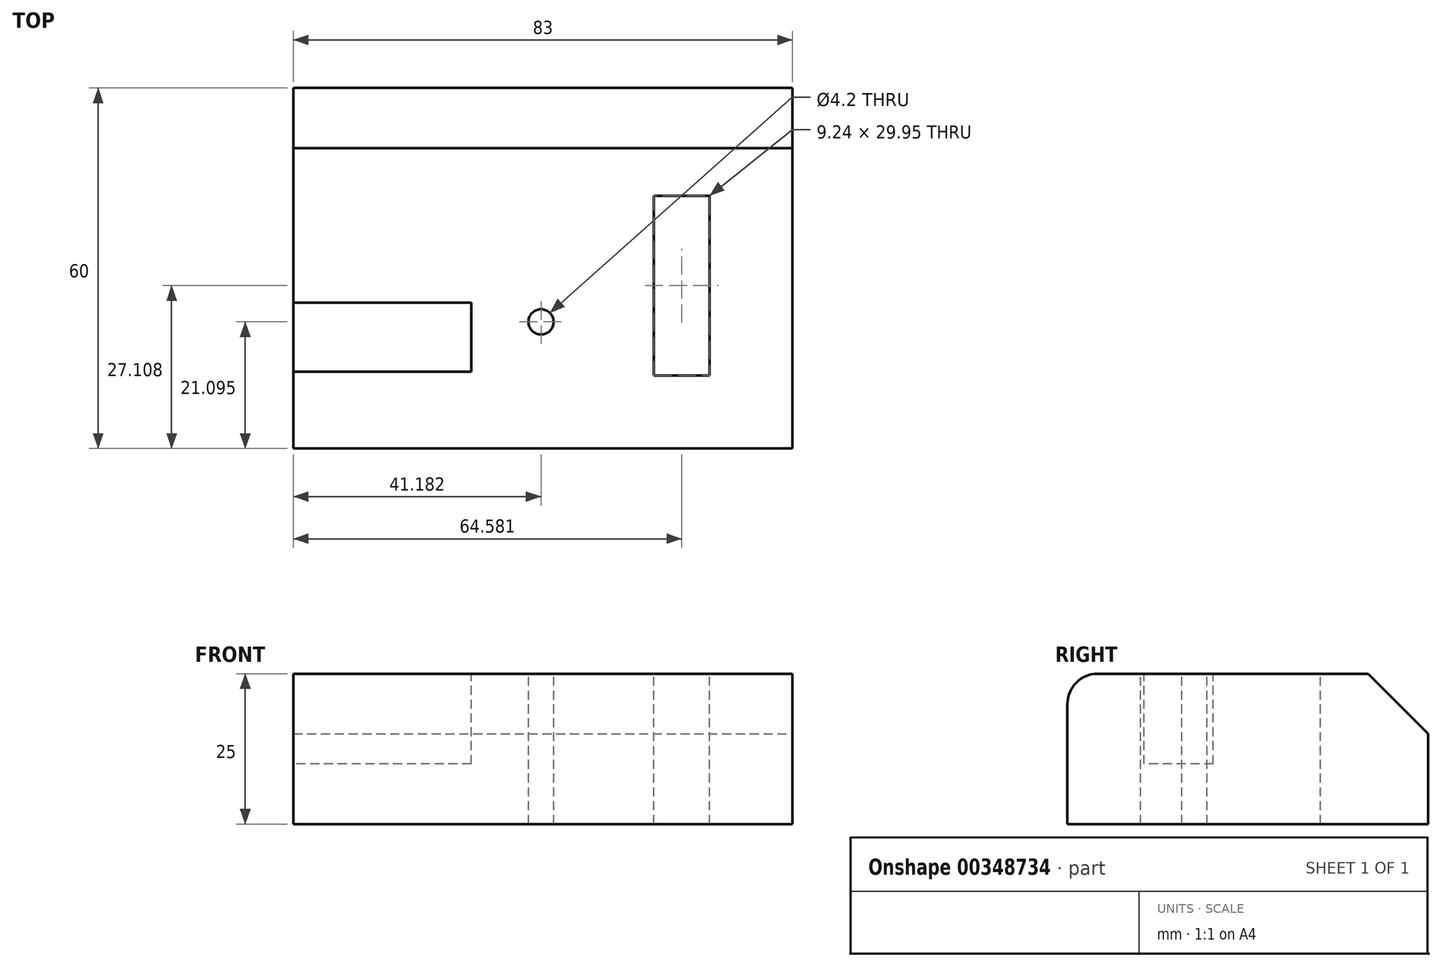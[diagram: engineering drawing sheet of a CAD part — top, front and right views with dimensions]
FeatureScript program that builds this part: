
annotation { "Feature Type Name" : "Feature", "Feature Type Description" : "" }
export const myFeature = defineFeature(function(context is Context, id is Id, definition is map)
    precondition{}
    {
        {
            var Q0;
            Q0=qCreatedBy(makeId("Top.planeOp"),FACE);
            var sketch = newSketch(context, id + "F0", { "sketchPlane" : qUnion([Q0])});
            skLineSegment(sketch, "E0.bottom", {"start": v(0, 60) * mm, "end": v(83, 60) * mm});
            skLineSegment(sketch, "E0.top", {"start": v(0, 0) * mm, "end": v(83, 0) * mm});
            skLineSegment(sketch, "E0.left", {"start": v(0, 60) * mm, "end": v(0, 0) * mm});
            skLineSegment(sketch, "E0.right", {"start": v(83, 60) * mm, "end": v(83, 0) * mm});
            skSolve(sketch);
        }
        {
            var Q0;
            Q0=makeQuery(id+"F0.imprint","IMPRINT",FACE,{"disambiguationData":[TD([[makeQuery(id+"F0.imprint","IMPRINT",EDGE,{"derivedFrom":sQuery(id+"F0.wireOp",EDGE,"E0.bottom")}),-1.0]])]});
            extrude(context, id + "F1", {"entities" : qUnion([Q0]), "depth" : 25 * mm});
        }
        {
            var Q0;
            Q0=makeQuery(id+"F1.opExtrude","CAP_EDGE",EDGE,{"disambiguationData":[OSD([sQuery(id+"F0.wireOp",EDGE,"E0.top")])],"isStart":false});
            fillet(context, id + "F2", {"entities" : qUnion([Q0]), "radius" : 5 * mm, "tangentPropagation" : true, "allowEdgeOverflow" : false});
        }
        {
            var Q0;
            Q0=makeQuery(id+"F1.opExtrude","CAP_EDGE",EDGE,{"disambiguationData":[OSD([sQuery(id+"F0.wireOp",EDGE,"E0.bottom")])],"isStart":false});
            chamfer(context, id + "F3", {"entities" : qUnion([Q0]), "width" : 10 * mm, "tangentPropagation" : true});
        }
        {
            var Q0;
            Q0=makeQuery(id+"F1.opExtrude","CAP_FACE",FACE,{"disambiguationData":[OSD([sQuery(id+"F0.wireOp",EDGE,"E0.bottom"),sQuery(id+"F0.wireOp",EDGE,"E0.top"),sQuery(id+"F0.wireOp",EDGE,"E0.left"),sQuery(id+"F0.wireOp",EDGE,"E0.right")])],"isStart":false});
            var sketch = newSketch(context, id + "F4", { "sketchPlane" : qUnion([Q0])});
            skPoint(sketch, "E1", {"position": v(41.18, 21.1) * mm});
            skSolve(sketch);
        }
        {
            var Q0;
            Q0=sQuery(id+"F4.wireOp",VERTEX,"E1");
            var Q1;
            Q1=makeQuery(id+"F1.opExtrude","SWEPT_BODY",BODY,{"disambiguationData":[OSD([sQuery(id+"F0.wireOp",EDGE,"E0.bottom"),sQuery(id+"F0.wireOp",EDGE,"E0.top"),sQuery(id+"F0.wireOp",EDGE,"E0.left"),sQuery(id+"F0.wireOp",EDGE,"E0.right")])]});
            hole(context, id + "F5", {"style" : HoleStyle.SIMPLE, "endStyle" : HoleEndStyle.THROUGH, "standardTappedOrClearance" : lookupTablePath({ "standard" : "ISO", "engagement" : "75%", "pitch" : "0.8 mm", "size" : "M5", "type" : "Tapped" }), "standardBlindInLast" : lookupTablePath({ "standard" : "ISO", "engagement" : "75%", "pitch" : "0.8 mm", "size" : "M5", "type" : "Tapped" }), "holeDiameter" : 4.2 * mm, "showTappedDepth" : true, "isTappedThrough" : true, "tappedDepth" : 12 * mm, "tapClearance" : 3, "locations" : qUnion([Q0]), "scope" : qUnion([Q1]), "majorDiameter" : 5 * mm});
        }
        {
            var Q0;
            Q0=makeQuery(id+"F1.opExtrude","CAP_FACE",FACE,{"disambiguationData":[OSD([sQuery(id+"F0.wireOp",EDGE,"E0.bottom"),sQuery(id+"F0.wireOp",EDGE,"E0.top"),sQuery(id+"F0.wireOp",EDGE,"E0.left"),sQuery(id+"F0.wireOp",EDGE,"E0.right")])],"isStart":false});
            var sketch = newSketch(context, id + "F6", { "sketchPlane" : qUnion([Q0])});
            skLineSegment(sketch, "E2.bottom", {"start": v(59.96, 12.14) * mm, "end": v(69.2, 12.14) * mm});
            skLineSegment(sketch, "E2.top", {"start": v(59.96, 42.08) * mm, "end": v(69.2, 42.08) * mm});
            skLineSegment(sketch, "E2.left", {"start": v(59.96, 12.14) * mm, "end": v(59.96, 42.08) * mm});
            skLineSegment(sketch, "E2.right", {"start": v(69.2, 12.14) * mm, "end": v(69.2, 42.08) * mm});
            skSolve(sketch);
        }
        {
            var Q0;
            Q0=makeQuery(id+"F6.imprint","IMPRINT",FACE,{"disambiguationData":[TD([[makeQuery(id+"F6.imprint","IMPRINT",EDGE,{"derivedFrom":sQuery(id+"F6.wireOp",EDGE,"E2.bottom")}),1.0]])]});
            extrude(context, id + "F7", {"entities" : qUnion([Q0]), "operationType" : NewBodyOperationType.REMOVE, "oppositeDirection" : true, "depth" : 30 * mm});
        }
        {
            var Q0;
            Q0=makeQuery(id+"F1.opExtrude","CAP_FACE",FACE,{"disambiguationData":[OSD([sQuery(id+"F0.wireOp",EDGE,"E0.bottom"),sQuery(id+"F0.wireOp",EDGE,"E0.top"),sQuery(id+"F0.wireOp",EDGE,"E0.left"),sQuery(id+"F0.wireOp",EDGE,"E0.right")])],"isStart":false});
            var sketch = newSketch(context, id + "F8", { "sketchPlane" : qUnion([Q0])});
            skLineSegment(sketch, "E3.bottom", {"start": v(29.59, 12.76) * mm, "end": v(0, 12.76) * mm});
            skLineSegment(sketch, "E3.top", {"start": v(29.59, 24.25) * mm, "end": v(0, 24.25) * mm});
            skLineSegment(sketch, "E3.left", {"start": v(29.59, 12.76) * mm, "end": v(29.59, 24.25) * mm});
            skLineSegment(sketch, "E3.right", {"start": v(0, 12.76) * mm, "end": v(0, 24.25) * mm});
            skSolve(sketch);
        }
        {
            var Q0;
            Q0 = qSketchRegion(id + "F8", true);
            extrude(context, id + "F9", {"entities" : qUnion([Q0]), "operationType" : NewBodyOperationType.REMOVE, "oppositeDirection" : true, "depth" : 15 * mm});
        }
    });
